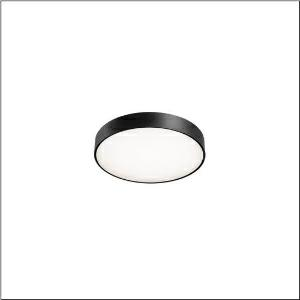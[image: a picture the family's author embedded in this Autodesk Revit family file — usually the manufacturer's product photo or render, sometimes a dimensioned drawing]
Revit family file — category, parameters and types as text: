
# Revit family: round_21_s_51mr34fd0321b
name_source: partatom
category: Lighting Fixtures
units: mm (PartAtom-declared; Revit-internal decimal feet)

## family parameters
Cut with Voids When Loaded = No
Host = Face
Light Source = No
Part Type = Normal
Room Calculation Point = No
Round Connector Dimension = Use Diameter
Shared = No

## types (1)
- Round 21 S (1 x LED, 3750 lm, 30.3 W, 3000K)
    Apparent Load = 30 VA
    CIE Flux Codes = 49 80 96 100 100
    Color Rendering = 80
    Color Temperature = 3000K
    Default Elevation = 1800 mm
    Description = Round 21 S, wall and ceiling luminaire, primary optical cover: cover, of PMMA, opal, light emission: direct distribution, primary light characteristic: symmetric, installation type: suspended mounting, surface-mounted, LED, rated luminous flux: 3.750lm, luminous efficacy: 124lm/W, light colour: 830, colour temperature: 3000K, control gear: DALI 2, with terminal, 5-pole, mains connection: 230V, AC, 50/60Hz, rated input power: 30.3W, housing, of aluminium, coated, black, diameter: 400mm, height: 62mm, protection rating (complete): IP40, insulation class (complete): insulation class I (protective earthing), certification: CE, impact resistance: IK04, permissible operating ambient temperature: -10..+35°C, packaging unit: 1 piece
    Height = 87 mm
    Lamp = 1 x LED
    Lamp Light Flux = 3750 lm
    Lamp Power = 30.3 W
    Lamp count = 1
    Length = 400 mm
    Luminous efficacy = 124 lm/W
    Manufacturer = Siteco
    ModVariant = No
    Model = 51MR34FD0321B
    Mounting Place = Wall
    Mounting Type = Surface mounted
    Number of Poles = 1
    OnlyDefault = Yes
    Power Factor = 1
    Product Name = Round 21 S
    Product group = wall and ceiling luminaire
    ProductGroupID = 2001
    Protection Class = Protection class I
    Protection Degree = IP 40
    RLX_Detail_Level = 1
    RLX_Emergency_Light_Flux = 0 lm
    RLX_Emergency_Type = 0
    RLX_Emergency_Type_DB = No
    RlxData = <blob elided: 13453 chars, md5=77dc256f>
    Socket = socket
    Standby Power = 0 W
    System Light Flux = 3750 lm
    System Power = 30 W
    Type Comments = Product without accessories
    Type Image = l_1258311.jpg
    URL = http://relux.com
    VarID = ---
    Voltage = 0 V
    Weight = 0.00 kg
    Width = 0 mm  [stored 0 ft]

note: [stored X ft] marks values corroborated as IEEE doubles in the binary element streams (Revit-internal decimal feet)

## geometry (parser evidence)
native form markers: Sweep x8
no freeform markers — native parametric forms only
